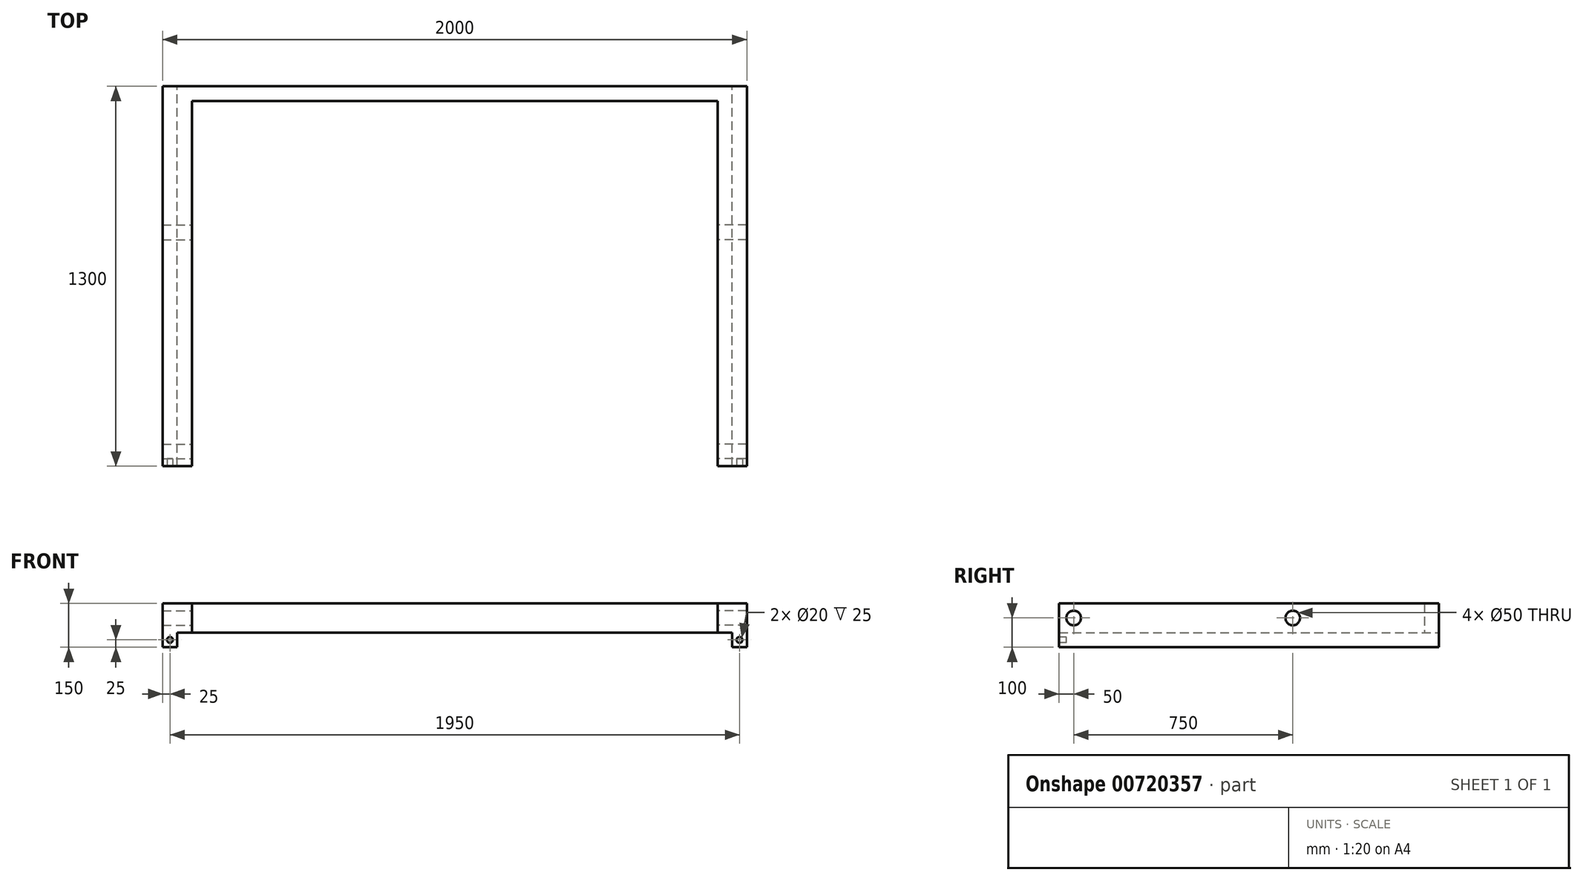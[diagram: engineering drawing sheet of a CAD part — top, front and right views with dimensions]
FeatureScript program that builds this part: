
annotation { "Feature Type Name" : "Feature", "Feature Type Description" : "" }
export const myFeature = defineFeature(function(context is Context, id is Id, definition is map)
    precondition{}
    {
        {
            var Q0;
            Q0=qCreatedBy(makeId("Right.planeOp"),FACE);
            var sketch = newSketch(context, id + "F0", { "sketchPlane" : qUnion([Q0])});
            skLineSegment(sketch, "E0.bottom", {"start": v(650, 75) * mm, "end": v(-650, 75) * mm});
            skLineSegment(sketch, "E0.top", {"start": v(650, -75) * mm, "end": v(-650, -75) * mm});
            skLineSegment(sketch, "E0.left", {"start": v(650, 75) * mm, "end": v(650, -75) * mm});
            skLineSegment(sketch, "E0.right", {"start": v(-650, 75) * mm, "end": v(-650, -75) * mm});
            skPoint(sketch, "E0.middle", {"position": v(0, 0) * mm});
            skSolve(sketch);
        }
        {
            var Q0;
            Q0=makeQuery(id+"F0.imprint","IMPRINT",FACE,{"disambiguationData":[TD([[makeQuery(id+"F0.imprint","IMPRINT",EDGE,{"derivedFrom":sQuery(id+"F0.wireOp",EDGE,"E0.bottom")}),1.0]])]});
            extrude(context, id + "F1", {"entities" : qUnion([Q0]), "depth" : 50 * mm, "offsetDistance" : 25 * mm});
        }
        {
            var Q0;
            Q0=makeQuery(id+"F1.opExtrude","CAP_FACE",FACE,{"disambiguationData":[OSD([sQuery(id+"F0.wireOp",EDGE,"E0.bottom"),sQuery(id+"F0.wireOp",EDGE,"E0.top"),sQuery(id+"F0.wireOp",EDGE,"E0.left"),sQuery(id+"F0.wireOp",EDGE,"E0.right")])],"isStart":false});
            var sketch = newSketch(context, id + "F2", { "sketchPlane" : qUnion([Q0])});
            skLineSegment(sketch, "E1", {"start": v(-650, -25) * mm, "end": v(650, -25) * mm});
            skSolve(sketch);
        }
        {
            var Q0;
            {var subQ0=sQuery(id+"F2.wireOp",EDGE,"E1");Q0=makeQuery(id+"F2.imprint","IMPRINT",FACE,{"disambiguationData":[TD([[makeQuery(id+"F2.imprint","IMPRINT",EDGE,{"derivedFrom":subQ0}),1.0]])]});}
            extrude(context, id + "F3", {"entities" : qUnion([Q0]), "operationType" : NewBodyOperationType.ADD, "depth" : 50 * mm, "offsetDistance" : 25 * mm});
        }
        {
            var Q0;
            Q0=makeQuery(id+"F3.opExtrude","CAP_FACE",FACE,{"disambiguationData":[OSD([sQuery(id+"F0.wireOp",EDGE,"E0.bottom"),sQuery(id+"F0.wireOp",EDGE,"E0.left"),sQuery(id+"F0.wireOp",EDGE,"E0.right"),sQuery(id+"F2.wireOp",EDGE,"E1")])],"isStart":false});
            var sketch = newSketch(context, id + "F4", { "sketchPlane" : qUnion([Q0])});
            skLineSegment(sketch, "E2", {"start": v(600, 75) * mm, "end": v(600, -25) * mm});
            skSolve(sketch);
        }
        {
            var Q0;
            {var subQ0=sQuery(id+"F4.wireOp",EDGE,"E2");Q0=makeQuery(id+"F4.imprint","IMPRINT",FACE,{"disambiguationData":[TD([[makeQuery(id+"F4.imprint","IMPRINT",EDGE,{"derivedFrom":subQ0}),1.0]])]});}
            extrude(context, id + "F5", {"entities" : qUnion([Q0]), "operationType" : NewBodyOperationType.ADD, "depth" : 1800 * mm, "offsetDistance" : 25 * mm});
        }
        {
            var Q0;
            Q0=makeQuery(id+"F5.opExtrude","CAP_FACE",FACE,{"disambiguationData":[OSD([sQuery(id+"F0.wireOp",EDGE,"E0.bottom"),sQuery(id+"F0.wireOp",EDGE,"E0.left"),sQuery(id+"F2.wireOp",EDGE,"E1"),sQuery(id+"F4.wireOp",EDGE,"E2")])],"isStart":false});
            extrude(context, id + "F6", {"entities" : qUnion([Q0]), "operationType" : NewBodyOperationType.ADD, "depth" : 100 * mm, "offsetDistance" : 25 * mm});
        }
        {
            var Q0;
            {var subQ0=sQuery(id+"F4.wireOp",EDGE,"E2");Q0=makeQuery(id+"F6.boolean.opBoolean","MERGE",FACE,{"derivedFrom":[makeQuery(id+"F5.opExtrude","SWEPT_FACE",FACE,{"disambiguationData":[OSD([subQ0])]}),makeQuery(id+"F6.opExtrude","SWEPT_FACE",FACE,{"disambiguationData":[OSD([subQ0])]})]});}
            var sketch = newSketch(context, id + "F7", { "sketchPlane" : qUnion([Q0])});
            skLineSegment(sketch, "E3", {"start": v(1900, 75) * mm, "end": v(1900, -25) * mm});
            skSolve(sketch);
        }
        {
            var Q0;
            {var subQ0=sQuery(id+"F7.wireOp",EDGE,"E3");Q0=makeQuery(id+"F7.imprint","IMPRINT",FACE,{"disambiguationData":[TD([[makeQuery(id+"F7.imprint","IMPRINT",EDGE,{"derivedFrom":subQ0}),1.0]])]});}
            extrude(context, id + "F8", {"entities" : qUnion([Q0]), "operationType" : NewBodyOperationType.ADD, "depth" : 1250 * mm, "offsetDistance" : 25 * mm});
        }
        {
            var Q0;
            {var subQ0=sQuery(id+"F2.wireOp",EDGE,"E1");Q0=makeQuery(id+"F8.boolean.opBoolean","MERGE",FACE,{"derivedFrom":[makeQuery(id+"F6.boolean.opBoolean","MERGE",FACE,{"derivedFrom":[makeQuery(id+"F5.boolean.opBoolean","MERGE",FACE,{"derivedFrom":[makeQuery(id+"F3.opExtrude","SWEPT_FACE",FACE,{"disambiguationData":[OSD([subQ0])]}),makeQuery(id+"F5.opExtrude","SWEPT_FACE",FACE,{"disambiguationData":[OSD([subQ0])]})]}),makeQuery(id+"F6.opExtrude","SWEPT_FACE",FACE,{"disambiguationData":[OSD([subQ0])]})]}),makeQuery(id+"F8.opExtrude","SWEPT_FACE",FACE,{"disambiguationData":[OSD([subQ0,sQuery(id+"F4.wireOp",EDGE,"E2")])]})]});}
            var sketch = newSketch(context, id + "F9", { "sketchPlane" : qUnion([Q0])});
            skLineSegment(sketch, "E4", {"start": v(1950, 650) * mm, "end": v(1950, -650) * mm});
            skSolve(sketch);
        }
        {
            var Q0;
            {var subQ0=sQuery(id+"F9.wireOp",EDGE,"E4");Q0=makeQuery(id+"F9.imprint","IMPRINT",FACE,{"disambiguationData":[TD([[makeQuery(id+"F9.imprint","IMPRINT",EDGE,{"derivedFrom":subQ0}),1.0]])]});}
            extrude(context, id + "F10", {"entities" : qUnion([Q0]), "operationType" : NewBodyOperationType.ADD, "depth" : 50 * mm, "offsetDistance" : 25 * mm});
        }
        {
            var Q0;
            Q0=makeQuery(id+"F3.opExtrude","CAP_FACE",FACE,{"disambiguationData":[OSD([sQuery(id+"F0.wireOp",EDGE,"E0.bottom"),sQuery(id+"F0.wireOp",EDGE,"E0.left"),sQuery(id+"F0.wireOp",EDGE,"E0.right"),sQuery(id+"F2.wireOp",EDGE,"E1")])],"isStart":false});
            var sketch = newSketch(context, id + "F11", { "sketchPlane" : qUnion([Q0])});
            skLineSegment(sketch, "E5", {"start": v(550, 75) * mm, "end": v(550, -25) * mm});
            skCircle(sketch, "E6", {"center": v(-600, 25) * mm, "radius": 25 * mm});
            skPoint(sketch, "E6.centerSnap0", {"position": v(-650, 25) * mm});
            skCircle(sketch, "E7", {"center": v(150, 25) * mm, "radius": 25 * mm});
            skPoint(sketch, "E7.centerSnap0", {"position": v(550, 25) * mm});
            skSolve(sketch);
        }
        {
            var Q0;
            Q0=makeQuery(id+"F11.imprint","IMPRINT",FACE,{"disambiguationData":[TD([[makeQuery(id+"F11.imprint","IMPRINT",EDGE,{"derivedFrom":sQuery(id+"F11.wireOp",EDGE,"E7")}),1.0]])]});
            var Q1;
            Q1=makeQuery(id+"F11.imprint","IMPRINT",FACE,{"disambiguationData":[TD([[makeQuery(id+"F11.imprint","IMPRINT",EDGE,{"derivedFrom":sQuery(id+"F11.wireOp",EDGE,"E6")}),1.0]])]});
            var Q2;
            Q2=sQuery(id+"F11.wireOp",EDGE,"E7");
            var Q3;
            Q3=sQuery(id+"F11.wireOp",EDGE,"E6");
            extrude(context, id + "F12", {"entities" : qUnion([Q0, Q1]), "operationType" : NewBodyOperationType.REMOVE, "surfaceEntities" : qUnion([Q2, Q3]), "oppositeDirection" : true, "depth" : 200 * mm, "offsetDistance" : 25 * mm});
        }
        {
            var Q0;
            Q0=makeQuery(id+"F8.opExtrude","SWEPT_FACE",FACE,{"disambiguationData":[OSD([sQuery(id+"F7.wireOp",EDGE,"E3")])]});
            var sketch = newSketch(context, id + "F13", { "sketchPlane" : qUnion([Q0])});
            skLineSegment(sketch, "E8", {"start": v(-550, -25) * mm, "end": v(-550, 75) * mm});
            skCircle(sketch, "E9", {"center": v(-150, 25) * mm, "radius": 25 * mm});
            skPoint(sketch, "E9.centerSnap0", {"position": v(-550, 25) * mm});
            skCircle(sketch, "E10", {"center": v(600, 25) * mm, "radius": 25 * mm});
            skPoint(sketch, "E10.centerSnap0", {"position": v(650, 25) * mm});
            skSolve(sketch);
        }
        {
            var Q0;
            Q0 = qSketchRegion(id + "F13", true);
            extrude(context, id + "F14", {"entities" : qUnion([Q0]), "operationType" : NewBodyOperationType.REMOVE, "oppositeDirection" : true, "depth" : 200 * mm, "offsetDistance" : 25 * mm});
        }
        {
            var Q0;
            {var subQ0=sQuery(id+"F0.wireOp",EDGE,"E0.right");Q0=makeQuery(id+"F3.boolean.opBoolean","MERGE",FACE,{"derivedFrom":[makeQuery(id+"F1.opExtrude","SWEPT_FACE",FACE,{"disambiguationData":[OSD([subQ0])]}),makeQuery(id+"F3.opExtrude","SWEPT_FACE",FACE,{"disambiguationData":[OSD([subQ0])]})]});}
            var sketch = newSketch(context, id + "F15", { "sketchPlane" : qUnion([Q0])});
            skCircle(sketch, "E11", {"center": v(25, -50) * mm, "radius": 10 * mm});
            skPoint(sketch, "E11.centerSnap0", {"position": v(50, -50) * mm});
            skPoint(sketch, "E11.centerSnap1", {"position": v(25, -75) * mm});
            skSolve(sketch);
        }
        {
            var Q0;
            Q0 = qSketchRegion(id + "F15", true);
            extrude(context, id + "F16", {"entities" : qUnion([Q0]), "operationType" : NewBodyOperationType.REMOVE, "oppositeDirection" : true, "depth" : 25 * mm, "offsetDistance" : 25 * mm});
        }
        {
            var Q0;
            {var subQ0=sQuery(id+"F4.wireOp",EDGE,"E2");var subQ1=sQuery(id+"F2.wireOp",EDGE,"E1");var subQ2=makeQuery(id+"F8.opExtrude","CAP_EDGE",EDGE,{"disambiguationData":[OSD([subQ1,subQ0])],"isStart":false});Q0=makeQuery(id+"F10.boolean.opBoolean","MERGE",FACE,{"derivedFrom":[makeQuery(id+"F8.opExtrude","CAP_FACE",FACE,{"disambiguationData":[OSD([sQuery(id+"F0.wireOp",EDGE,"E0.bottom"),subQ1,subQ0,sQuery(id+"F7.wireOp",EDGE,"E3")])],"isStart":false}),makeQuery(id+"F10.opExtrude","SWEPT_FACE",FACE,{"disambiguationData":[OSD([subQ1,subQ0]),TDD([makeQuery(id+"F9.imprint","IMPRINT",EDGE,{"disambiguationData":[TD([[makeQuery(id+"F9.imprint","INTERSECT",VERTEX,{"derivedFrom":[subQ2,sQuery(id+"F9.wireOp",EDGE,"E4")]}),1.0]])],"derivedFrom":subQ2})])]})]});}
            var sketch = newSketch(context, id + "F17", { "sketchPlane" : qUnion([Q0])});
            skCircle(sketch, "E12", {"center": v(1975, -50) * mm, "radius": 10 * mm});
            skPoint(sketch, "E12.centerSnap0", {"position": v(1950, -50) * mm});
            skPoint(sketch, "E12.centerSnap1", {"position": v(1975, -75) * mm});
            skSolve(sketch);
        }
        {
            var Q0;
            Q0 = qSketchRegion(id + "F17", true);
            extrude(context, id + "F18", {"entities" : qUnion([Q0]), "operationType" : NewBodyOperationType.REMOVE, "oppositeDirection" : true, "depth" : 25 * mm, "offsetDistance" : 25 * mm});
        }
    });
